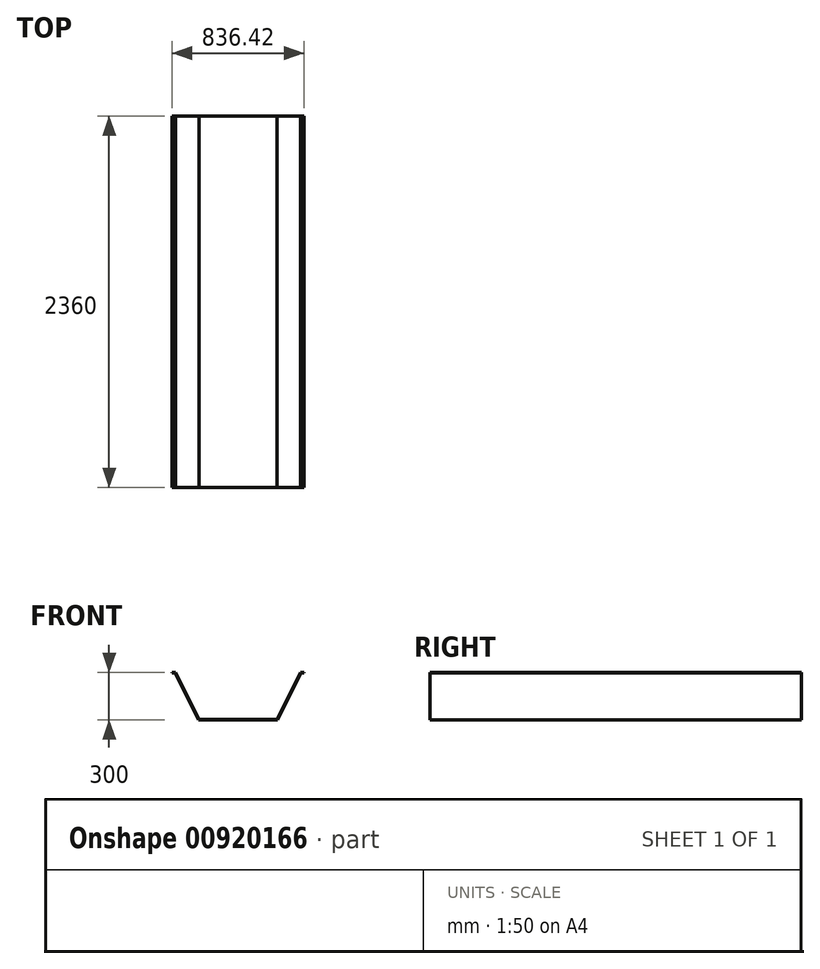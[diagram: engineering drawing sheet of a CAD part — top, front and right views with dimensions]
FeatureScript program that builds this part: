
annotation { "Feature Type Name" : "Feature", "Feature Type Description" : "" }
export const myFeature = defineFeature(function(context is Context, id is Id, definition is map)
    precondition{}
    {
        {
            var Q0;
            Q0=qCreatedBy(makeId("Front.planeOp"),FACE);
            var sketch = newSketch(context, id + "F0", { "sketchPlane" : qUnion([Q0])});
            skLineSegment(sketch, "E0", {"start": v(0, 0) * mm, "end": v(500, 0) * mm});
            skLineSegment(sketch, "E1", {"start": v(649.2, 298.4) * mm, "end": v(500, 0) * mm});
            skLineSegment(sketch, "E2", {"start": v(-149.2, 298.4) * mm, "end": v(0, 0) * mm});
            skLineSegment(sketch, "E3", {"start": v(-150, 300) * mm, "end": v(-148.21, 300) * mm});
            skLineSegment(sketch, "E4.0", {"start": v(-148.21, 300) * mm, "end": v(0.99, 1.6) * mm});
            skLineSegment(sketch, "E5.0", {"start": v(0.99, 1.6) * mm, "end": v(499.01, 1.6) * mm});
            skLineSegment(sketch, "E6.trimOffspring", {"start": v(648.21, 300) * mm, "end": v(650, 300) * mm});
            skLineSegment(sketch, "E7.0", {"start": v(648.21, 300) * mm, "end": v(499.01, 1.6) * mm});
            skLineSegment(sketch, "E8", {"start": v(-148.21, 300) * mm, "end": v(-168.21, 300) * mm});
            skLineSegment(sketch, "E9", {"start": v(-168.21, 300) * mm, "end": v(-168.21, 298.4) * mm});
            skLineSegment(sketch, "E10", {"start": v(-168.21, 298.4) * mm, "end": v(-149.2, 298.4) * mm});
            skLineSegment(sketch, "E11", {"start": v(648.21, 300) * mm, "end": v(668.21, 300) * mm});
            skLineSegment(sketch, "E12", {"start": v(668.21, 300) * mm, "end": v(668.21, 298.4) * mm});
            skLineSegment(sketch, "E13", {"start": v(668.21, 298.4) * mm, "end": v(649.2, 298.4) * mm});
            skSolve(sketch);
        }
        {
            var Q0;
            Q0 = qSketchRegion(id + "F0", true);
            extrude(context, id + "F1", {"entities" : qUnion([Q0]), "depth" : 2360 * mm, "offsetDistance" : 25 * mm});
        }
    });
